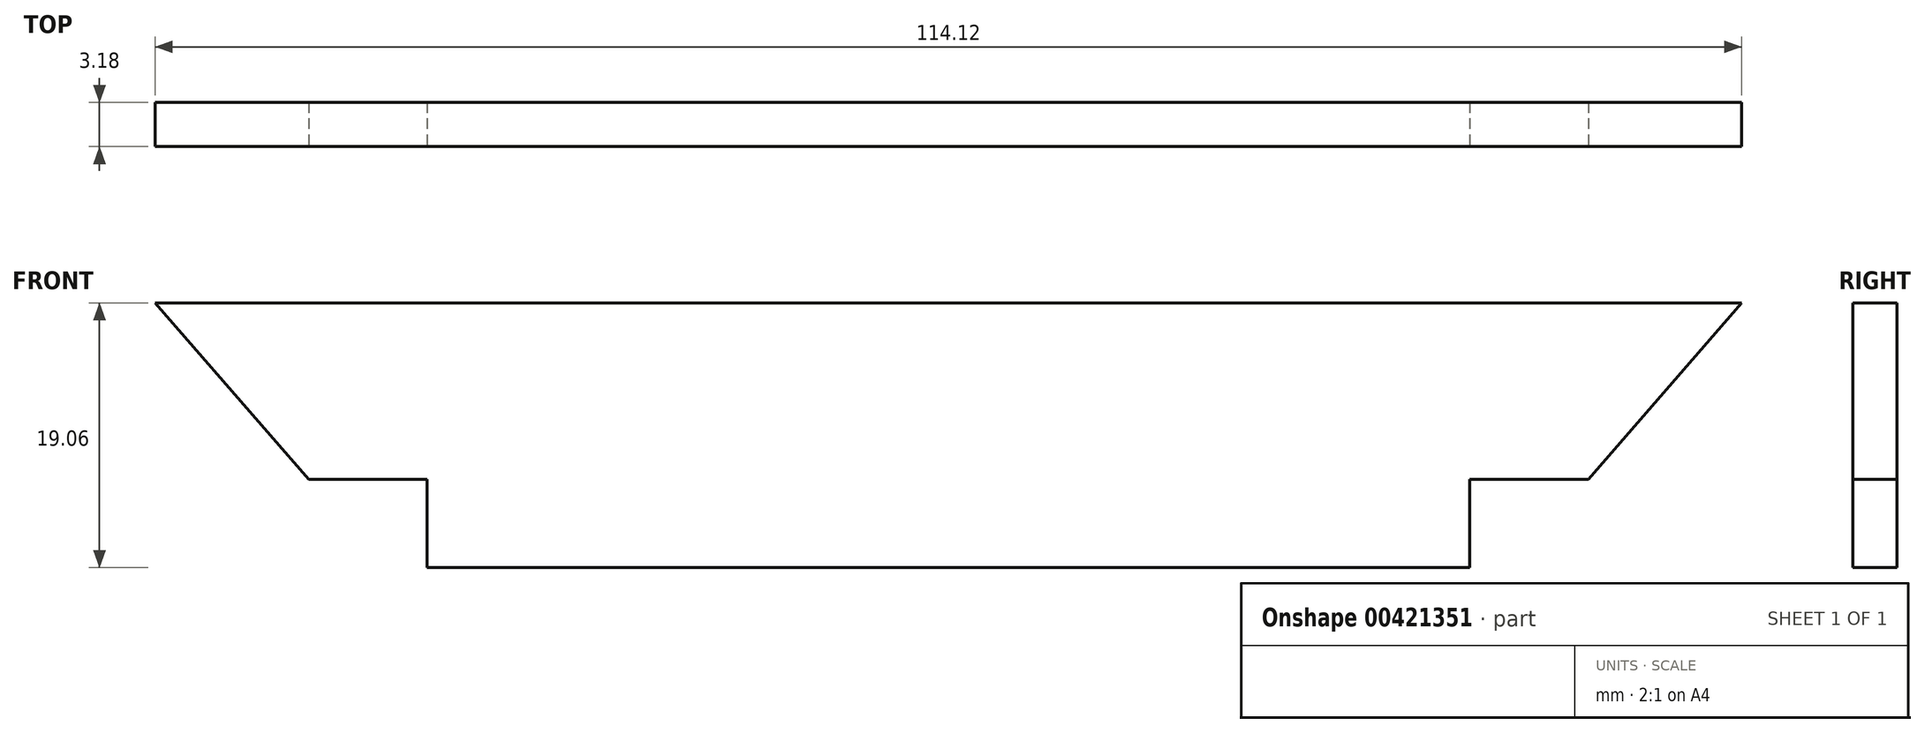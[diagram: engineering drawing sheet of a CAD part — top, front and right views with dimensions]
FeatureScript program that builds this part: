
annotation { "Feature Type Name" : "Feature", "Feature Type Description" : "" }
export const myFeature = defineFeature(function(context is Context, id is Id, definition is map)
    precondition{}
    {
        {
            var Q0;
            Q0=qCreatedBy(makeId("Front.planeOp"),FACE);
            var sketch = newSketch(context, id + "F0", { "sketchPlane" : qUnion([Q0])});
            skLineSegment(sketch, "E0.bottom", {"start": v(-40.5, 9.53) * mm, "end": v(40.5, 9.53) * mm});
            skLineSegment(sketch, "E0.top", {"start": v(-40.5, -9.53) * mm, "end": v(40.5, -9.53) * mm});
            skLineSegment(sketch, "E0.left", {"start": v(-40.5, 9.53) * mm, "end": v(-40.5, -9.53) * mm});
            skLineSegment(sketch, "E0.right", {"start": v(40.5, 9.53) * mm, "end": v(40.5, -9.53) * mm});
            skPoint(sketch, "E0.middle", {"position": v(0, 0) * mm});
            skSolve(sketch);
        }
        {
            var Q0;
            Q0 = qSketchRegion(id + "F0", true);
            extrude(context, id + "F1", {"entities" : qUnion([Q0]), "depth" : 3.17 * mm, "offsetDistance" : 25.4 * mm});
        }
        {
            var Q0;
            Q0=makeQuery(id+"F1.opExtrude","CAP_FACE",FACE,{"disambiguationData":[OSD([sQuery(id+"F0.wireOp",EDGE,"E0.bottom"),sQuery(id+"F0.wireOp",EDGE,"E0.top"),sQuery(id+"F0.wireOp",EDGE,"E0.left"),sQuery(id+"F0.wireOp",EDGE,"E0.right")])],"isStart":false});
            var sketch = newSketch(context, id + "F2", { "sketchPlane" : qUnion([Q0])});
            skLineSegment(sketch, "E1", {"start": v(-40.5, -9.53) * mm, "end": v(-86.2, 43.04) * mm, "construction": true});
            skLineSegment(sketch, "E2", {"start": v(-40.5, 9.53) * mm, "end": v(-57.06, 9.53) * mm});
            skLineSegment(sketch, "E3", {"start": v(-40.5, -9.53) * mm, "end": v(-57.06, 9.53) * mm});
            skLineSegment(sketch, "E4", {"start": v(0, 0) * mm, "end": v(0, 23.13) * mm, "construction": true});
            skLineSegment(sketch, "E5.MirrorCS", {"start": v(40.5, 9.53) * mm, "end": v(57.06, 9.53) * mm});
            skLineSegment(sketch, "E6.MirrorCS", {"start": v(40.5, -9.53) * mm, "end": v(86.2, 43.04) * mm, "construction": true});
            skLineSegment(sketch, "E7", {"start": v(-40.5, -9.53) * mm, "end": v(-40.5, 9.53) * mm});
            skLineSegment(sketch, "E8", {"start": v(40.5, -9.53) * mm, "end": v(57.06, 9.53) * mm});
            skLineSegment(sketch, "E9", {"start": v(40.5, -9.53) * mm, "end": v(40.5, 9.53) * mm});
            skSolve(sketch);
        }
        {
            var Q0;
            Q0 = qSketchRegion(id + "F2", true);
            extrude(context, id + "F3", {"entities" : qUnion([Q0]), "operationType" : NewBodyOperationType.ADD, "oppositeDirection" : true, "depth" : 3.17 * mm, "offsetDistance" : 25.4 * mm});
        }
        {
            var Q0;
            Q0=makeQuery(id+"F3.boolean.opBoolean","MERGE",FACE,{"derivedFrom":[makeQuery(id+"F1.opExtrude","CAP_FACE",FACE,{"disambiguationData":[OSD([sQuery(id+"F0.wireOp",EDGE,"E0.bottom"),sQuery(id+"F0.wireOp",EDGE,"E0.top"),sQuery(id+"F0.wireOp",EDGE,"E0.left"),sQuery(id+"F0.wireOp",EDGE,"E0.right")])],"isStart":false}),makeQuery(id+"F3.opExtrude","CAP_FACE",FACE,{"disambiguationData":[OSD([sQuery(id+"F2.wireOp",EDGE,"E2"),sQuery(id+"F2.wireOp",EDGE,"E3"),sQuery(id+"F2.wireOp",EDGE,"E7")])],"isStart":true}),makeQuery(id+"F3.opExtrude","CAP_FACE",FACE,{"disambiguationData":[OSD([sQuery(id+"F2.wireOp",EDGE,"E5.MirrorCS"),sQuery(id+"F2.wireOp",EDGE,"E8"),sQuery(id+"F2.wireOp",EDGE,"E9")])],"isStart":true})]});
            var sketch = newSketch(context, id + "F4", { "sketchPlane" : qUnion([Q0])});
            skLineSegment(sketch, "E10", {"start": v(0, 0) * mm, "end": v(0, -9.53) * mm, "construction": true});
            skLineSegment(sketch, "E11", {"start": v(-37.5, -9.53) * mm, "end": v(-37.5, -3.18) * mm});
            skLineSegment(sketch, "E12", {"start": v(-37.5, -3.18) * mm, "end": v(-46.02, -3.18) * mm});
            skLineSegment(sketch, "E13", {"start": v(-46.02, -3.18) * mm, "end": v(-40.5, -9.53) * mm});
            skLineSegment(sketch, "E14", {"start": v(-40.5, -9.53) * mm, "end": v(-37.5, -9.53) * mm});
            skLineSegment(sketch, "E15.MirrorCS", {"start": v(37.5, -3.17) * mm, "end": v(46.02, -3.17) * mm});
            skLineSegment(sketch, "E16.MirrorCS", {"start": v(46.02, -3.17) * mm, "end": v(40.5, -9.52) * mm});
            skLineSegment(sketch, "E17.MirrorCS", {"start": v(40.5, -9.52) * mm, "end": v(37.5, -9.52) * mm});
            skLineSegment(sketch, "E18.MirrorCS", {"start": v(37.5, -9.52) * mm, "end": v(37.5, -3.17) * mm});
            skSolve(sketch);
        }
        {
            var Q0;
            Q0 = qSketchRegion(id + "F4", true);
            extrude(context, id + "F5", {"entities" : qUnion([Q0]), "operationType" : NewBodyOperationType.REMOVE, "oppositeDirection" : true, "depth" : 25.4 * mm, "offsetDistance" : 25.4 * mm});
        }
    });
